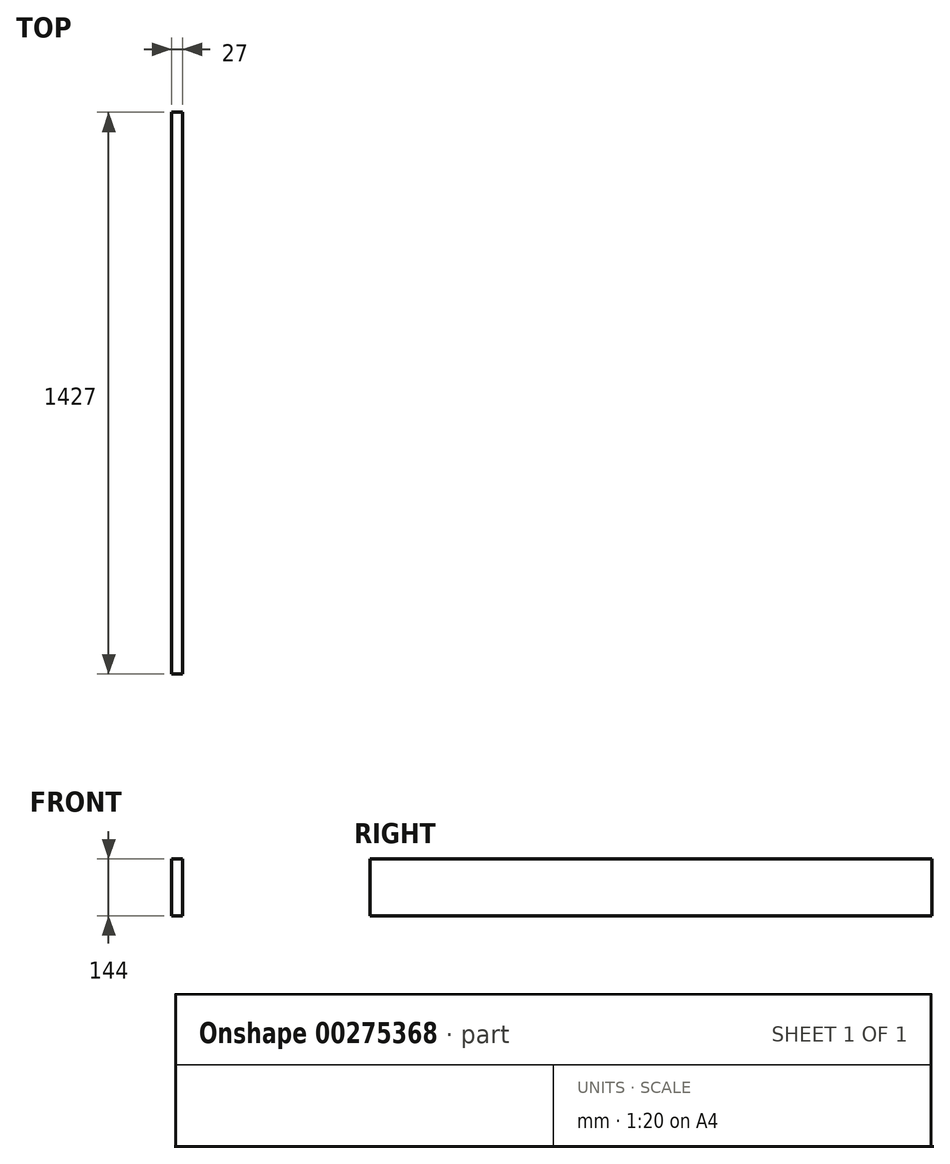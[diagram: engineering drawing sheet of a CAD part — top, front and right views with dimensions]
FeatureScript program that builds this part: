
annotation { "Feature Type Name" : "Feature", "Feature Type Description" : "" }
export const myFeature = defineFeature(function(context is Context, id is Id, definition is map)
    precondition{}
    {
        {
            var Q0;
            Q0=qCreatedBy(makeId("Front.planeOp"),FACE);
            var sketch = newSketch(context, id + "F0", { "sketchPlane" : qUnion([Q0])});
            skLineSegment(sketch, "E0.bottom", {"start": v(-13.5, 72) * mm, "end": v(13.5, 72) * mm});
            skLineSegment(sketch, "E0.top", {"start": v(-13.5, -72) * mm, "end": v(13.5, -72) * mm});
            skLineSegment(sketch, "E0.left", {"start": v(-13.5, 72) * mm, "end": v(-13.5, -72) * mm});
            skLineSegment(sketch, "E0.right", {"start": v(13.5, 72) * mm, "end": v(13.5, -72) * mm});
            skPoint(sketch, "E1", {"position": v(0, 72) * mm});
            skPoint(sketch, "E2", {"position": v(-13.5, 0) * mm});
            skSolve(sketch);
        }
        {
            var Q0;
            Q0=makeQuery(id+"F0.imprint","IMPRINT",FACE,{"disambiguationData":[TD([[makeQuery(id+"F0.imprint","IMPRINT",EDGE,{"derivedFrom":sQuery(id+"F0.wireOp",EDGE,"E0.bottom")}),-1.0]])]});
            extrude(context, id + "F1", {"entities" : qUnion([Q0]), "endBound" : BoundingType.SYMMETRIC, "depth" : 1427 * mm});
        }
    });
